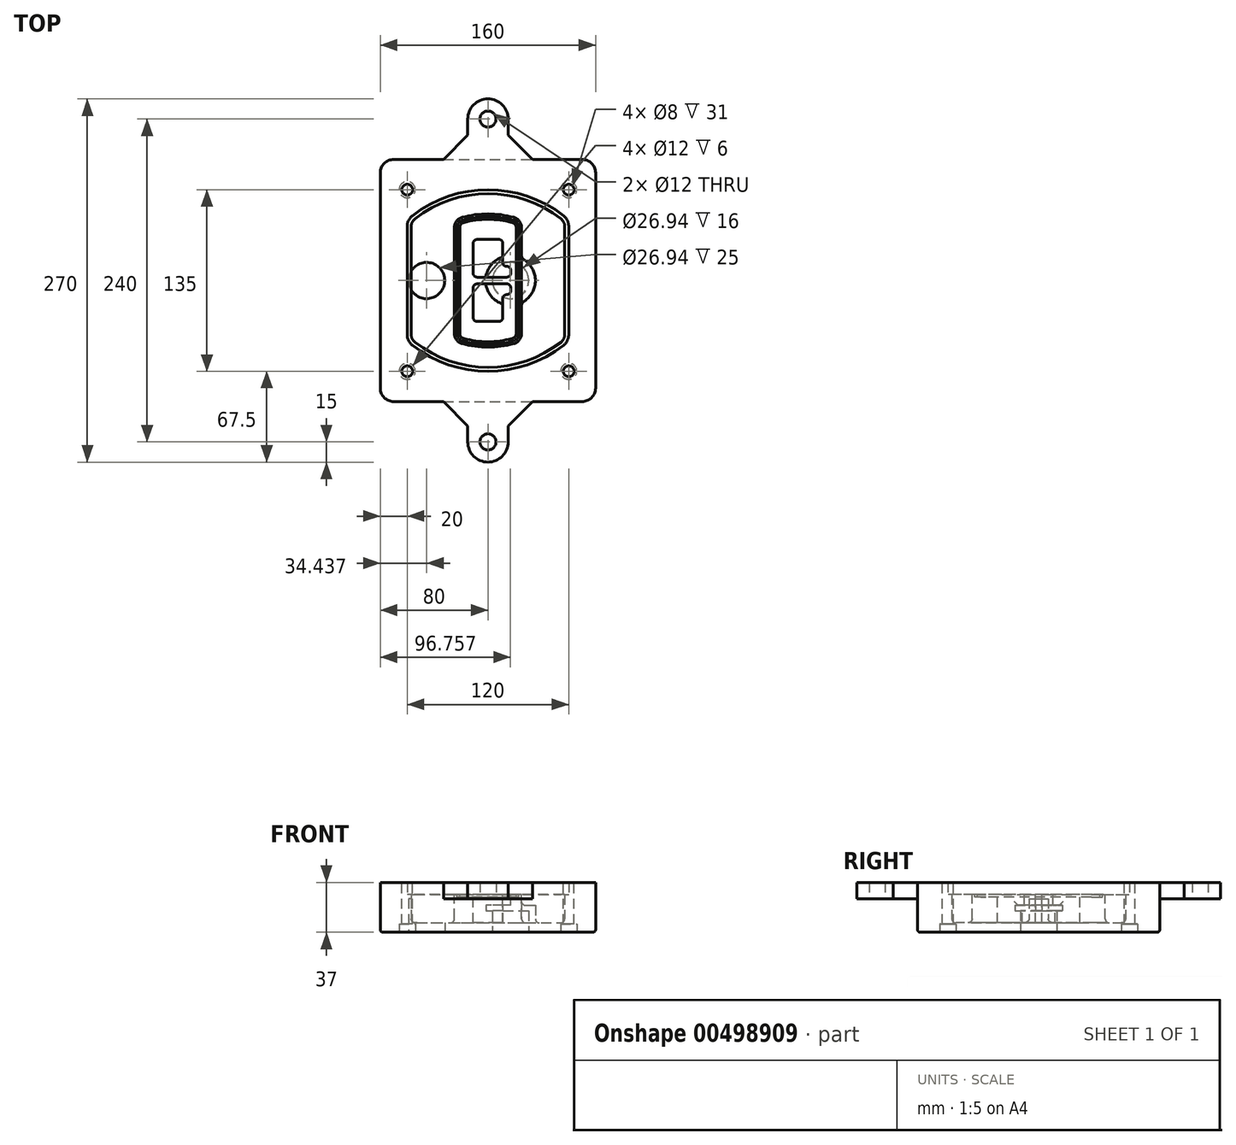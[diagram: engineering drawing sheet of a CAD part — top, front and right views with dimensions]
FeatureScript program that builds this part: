
annotation { "Feature Type Name" : "Feature", "Feature Type Description" : "" }
export const myFeature = defineFeature(function(context is Context, id is Id, definition is map)
    precondition{}
    {
        {
            var Q0;
            Q0=qCreatedBy(makeId("Top.planeOp"),FACE);
            var sketch = newSketch(context, id + "F0", { "sketchPlane" : qUnion([Q0])});
            skPoint(sketch, "E0.rect.middle", {"position": v(0, 0) * mm});
            skLineSegment(sketch, "E1.bottom", {"start": v(-70, -90) * mm, "end": v(70, -90) * mm});
            skLineSegment(sketch, "E1.top", {"start": v(-70, 90) * mm, "end": v(70, 90) * mm});
            skLineSegment(sketch, "E1.left", {"start": v(-80, -80) * mm, "end": v(-80, 80) * mm});
            skLineSegment(sketch, "E1.right", {"start": v(80, -80) * mm, "end": v(80, 80) * mm});
            skLineSegment(sketch, "E2", {"start": v(-80, 90) * mm, "end": v(80, -90) * mm, "construction": true});
            skLineSegment(sketch, "E3", {"start": v(80, 90) * mm, "end": v(-80, -90) * mm, "construction": true});
            skCircle(sketch, "E4", {"center": v(-60, 67.5) * mm, "radius": 4 * mm});
            skCircle(sketch, "E5", {"center": v(60, 67.5) * mm, "radius": 4 * mm});
            skCircle(sketch, "E6", {"center": v(60, -67.5) * mm, "radius": 4 * mm});
            skCircle(sketch, "E7", {"center": v(-60, -67.5) * mm, "radius": 4 * mm});
            skLineSegment(sketch, "E8", {"start": v(-60, 67.5) * mm, "end": v(60, 67.5) * mm, "construction": true});
            skLineSegment(sketch, "E9", {"start": v(60, 67.5) * mm, "end": v(60, -67.5) * mm, "construction": true});
            skLineSegment(sketch, "E10", {"start": v(60, -67.5) * mm, "end": v(-60, -67.5) * mm, "construction": true});
            skLineSegment(sketch, "E11", {"start": v(-60, -67.5) * mm, "end": v(-60, 67.5) * mm, "construction": true});
            skLineSegment(sketch, "E12", {"start": v(-60, 40.3) * mm, "end": v(-60, -40.3) * mm});
            skLineSegment(sketch, "E13", {"start": v(60, 40.3) * mm, "end": v(60, -40.3) * mm});
            skArc(sketch, "E14", {"start": v(56.15, 48.18) * mm, "mid": v(0, 67.5) * mm, "end": v(-56.15, 48.18) * mm});
            skArc(sketch, "E15", {"start": v(-56.15, -48.18) * mm, "mid": v(0, -67.5) * mm, "end": v(56.15, -48.18) * mm});
            skLineSegment(sketch, "E16", {"start": v(-60, 0) * mm, "end": v(60, 0) * mm, "construction": true});
            skPoint(sketch, "E17.visualSharp", {"position": v(-60, -45) * mm});
            skArc(sketch, "E17.filletArc", {"start": v(-60, -40.3) * mm, "mid": v(-58.99, -44.68) * mm, "end": v(-56.15, -48.18) * mm});
            skPoint(sketch, "E18.visualSharp", {"position": v(-60, 45) * mm});
            skArc(sketch, "E18.filletArc", {"start": v(-56.15, 48.18) * mm, "mid": v(-58.99, 44.68) * mm, "end": v(-60, 40.3) * mm});
            skPoint(sketch, "E19.visualSharp", {"position": v(60, 45) * mm});
            skArc(sketch, "E19.filletArc", {"start": v(60, 40.3) * mm, "mid": v(58.99, 44.68) * mm, "end": v(56.15, 48.18) * mm});
            skPoint(sketch, "E20.visualSharp", {"position": v(60, -45) * mm});
            skArc(sketch, "E20.filletArc", {"start": v(56.15, -48.18) * mm, "mid": v(58.99, -44.68) * mm, "end": v(60, -40.3) * mm});
            skPoint(sketch, "E21.visualSharp", {"position": v(-80, 90) * mm});
            skArc(sketch, "E21.filletArc", {"start": v(-70, 90) * mm, "mid": v(-77.07, 87.07) * mm, "end": v(-80, 80) * mm});
            skPoint(sketch, "E22.visualSharp", {"position": v(80, 90) * mm});
            skArc(sketch, "E22.filletArc", {"start": v(80, 80) * mm, "mid": v(77.07, 87.07) * mm, "end": v(70, 90) * mm});
            skPoint(sketch, "E23.visualSharp", {"position": v(80, -90) * mm});
            skArc(sketch, "E23.filletArc", {"start": v(70, -90) * mm, "mid": v(77.07, -87.07) * mm, "end": v(80, -80) * mm});
            skPoint(sketch, "E24.visualSharp", {"position": v(-80, -90) * mm});
            skArc(sketch, "E24.filletArc", {"start": v(-80, -80) * mm, "mid": v(-77.07, -87.07) * mm, "end": v(-70, -90) * mm});
            skArc(sketch, "E25.0", {"start": v(57, 40.3) * mm, "mid": v(56.3, 43.36) * mm, "end": v(54.3, 45.81) * mm});
            skLineSegment(sketch, "E25.1", {"start": v(57, 40.3) * mm, "end": v(57, -40.3) * mm});
            skArc(sketch, "E25.2", {"start": v(54.3, -45.81) * mm, "mid": v(56.3, -43.36) * mm, "end": v(57, -40.3) * mm});
            skArc(sketch, "E25.3", {"start": v(-54.3, -45.81) * mm, "mid": v(0, -64.5) * mm, "end": v(54.3, -45.81) * mm});
            skArc(sketch, "E25.4", {"start": v(-57, -40.3) * mm, "mid": v(-56.3, -43.36) * mm, "end": v(-54.3, -45.81) * mm});
            skArc(sketch, "E25.5", {"start": v(54.3, 45.81) * mm, "mid": v(0, 64.5) * mm, "end": v(-54.3, 45.81) * mm});
            skLineSegment(sketch, "E25.6", {"start": v(-57, 40.3) * mm, "end": v(-57, -40.3) * mm});
            skArc(sketch, "E25.7", {"start": v(-54.3, 45.81) * mm, "mid": v(-56.3, 43.36) * mm, "end": v(-57, 40.3) * mm});
            skArc(sketch, "E26.0", {"start": v(-58.62, 51.33) * mm, "mid": v(-62.58, 46.43) * mm, "end": v(-64, 40.3) * mm});
            skArc(sketch, "E26.1", {"start": v(58.62, 51.33) * mm, "mid": v(0, 71.5) * mm, "end": v(-58.62, 51.33) * mm});
            skArc(sketch, "E26.2", {"start": v(64, 40.3) * mm, "mid": v(62.58, 46.43) * mm, "end": v(58.62, 51.33) * mm});
            skLineSegment(sketch, "E26.3", {"start": v(64, 40.3) * mm, "end": v(64, -40.3) * mm});
            skArc(sketch, "E26.4", {"start": v(58.62, -51.33) * mm, "mid": v(62.58, -46.43) * mm, "end": v(64, -40.3) * mm});
            skLineSegment(sketch, "E26.5", {"start": v(-64, 40.3) * mm, "end": v(-64, -40.3) * mm});
            skArc(sketch, "E26.6", {"start": v(-58.62, -51.33) * mm, "mid": v(0, -71.5) * mm, "end": v(58.62, -51.33) * mm});
            skArc(sketch, "E26.7", {"start": v(-64, -40.3) * mm, "mid": v(-62.58, -46.43) * mm, "end": v(-58.62, -51.33) * mm});
            skSolve(sketch);
        }
        {
            var Q0;
            Q0=makeQuery(id+"F0.imprint","IMPRINT",FACE,{"disambiguationData":[TD([[makeQuery(id+"F0.imprint","IMPRINT",EDGE,{"derivedFrom":sQuery(id+"F0.wireOp",EDGE,"E1.bottom")}),1.0]])]});
            var Q1;
            Q1=makeQuery(id+"F0.imprint","IMPRINT",FACE,{"disambiguationData":[TD([[makeQuery(id+"F0.imprint","IMPRINT",EDGE,{"derivedFrom":sQuery(id+"F0.wireOp",EDGE,"E12")}),1.0]])]});
            var Q2;
            Q2=makeQuery(id+"F0.imprint","IMPRINT",FACE,{"disambiguationData":[TD([[makeQuery(id+"F0.imprint","IMPRINT",EDGE,{"derivedFrom":sQuery(id+"F0.wireOp",EDGE,"E25.0")}),1.0]])]});
            var Q3;
            Q3=makeQuery(id+"F0.imprint","IMPRINT",FACE,{"disambiguationData":[TD([[makeQuery(id+"F0.imprint","IMPRINT",EDGE,{"derivedFrom":sQuery(id+"F0.wireOp",EDGE,"E12")}),-1.0]])]});
            extrude(context, id + "F1", {"entities" : qUnion([Q0, Q1, Q2, Q3]), "oppositeDirection" : true, "depth" : 25 * mm});
        }
        {
            var Q0;
            Q0=makeQuery(id+"F0.imprint","IMPRINT",FACE,{"disambiguationData":[TD([[makeQuery(id+"F0.imprint","IMPRINT",EDGE,{"derivedFrom":sQuery(id+"F0.wireOp",EDGE,"E12")}),1.0]])]});
            extrude(context, id + "F2", {"entities" : qUnion([Q0]), "operationType" : NewBodyOperationType.ADD, "depth" : 3 * mm});
        }
        {
            var Q0;
            Q0=makeQuery(id+"F0.imprint","IMPRINT",FACE,{"disambiguationData":[TD([[makeQuery(id+"F0.imprint","IMPRINT",EDGE,{"derivedFrom":sQuery(id+"F0.wireOp",EDGE,"E25.0")}),1.0]])]});
            extrude(context, id + "F3", {"entities" : qUnion([Q0]), "operationType" : NewBodyOperationType.REMOVE, "oppositeDirection" : true, "depth" : 18 * mm});
        }
        {
            var Q0;
            Q0=makeQuery(id+"F2.opExtrude","CAP_FACE",FACE,{"disambiguationData":[OSD([sQuery(id+"F0.wireOp",EDGE,"E12"),sQuery(id+"F0.wireOp",EDGE,"E13"),sQuery(id+"F0.wireOp",EDGE,"E14"),sQuery(id+"F0.wireOp",EDGE,"E15"),sQuery(id+"F0.wireOp",EDGE,"E17.filletArc"),sQuery(id+"F0.wireOp",EDGE,"E18.filletArc"),sQuery(id+"F0.wireOp",EDGE,"E19.filletArc"),sQuery(id+"F0.wireOp",EDGE,"E20.filletArc"),sQuery(id+"F0.wireOp",EDGE,"E25.0"),sQuery(id+"F0.wireOp",EDGE,"E25.1"),sQuery(id+"F0.wireOp",EDGE,"E25.2"),sQuery(id+"F0.wireOp",EDGE,"E25.3"),sQuery(id+"F0.wireOp",EDGE,"E25.4"),sQuery(id+"F0.wireOp",EDGE,"E25.5"),sQuery(id+"F0.wireOp",EDGE,"E25.6"),sQuery(id+"F0.wireOp",EDGE,"E25.7")])],"isStart":false});
            var sketch = newSketch(context, id + "F4", { "sketchPlane" : qUnion([Q0])});
            skArc(sketch, "E27.0", {"start": v(-19.08, -46.97) * mm, "mid": v(0, -49.5) * mm, "end": v(19.08, -46.97) * mm});
            skArc(sketch, "E28.0", {"start": v(19.08, 46.97) * mm, "mid": v(0, 49.5) * mm, "end": v(-19.08, 46.97) * mm});
            skLineSegment(sketch, "E29", {"start": v(-25, 39.25) * mm, "end": v(-25, -39.25) * mm});
            skLineSegment(sketch, "E30", {"start": v(25, 39.25) * mm, "end": v(25, -39.25) * mm});
            skLineSegment(sketch, "E31", {"start": v(-25, 45.1) * mm, "end": v(25, 45.1) * mm, "construction": true});
            skLineSegment(sketch, "E32", {"start": v(-25, -45.1) * mm, "end": v(25, -45.1) * mm, "construction": true});
            skPoint(sketch, "E33.visualSharp", {"position": v(-25, 45.1) * mm});
            skArc(sketch, "E33.filletArc", {"start": v(-19.08, 46.97) * mm, "mid": v(-23.35, 44.11) * mm, "end": v(-25, 39.25) * mm});
            skPoint(sketch, "E34.visualSharp", {"position": v(25, 45.1) * mm});
            skArc(sketch, "E34.filletArc", {"start": v(25, 39.25) * mm, "mid": v(23.35, 44.11) * mm, "end": v(19.08, 46.97) * mm});
            skPoint(sketch, "E35.visualSharp", {"position": v(25, -45.1) * mm});
            skArc(sketch, "E35.filletArc", {"start": v(19.08, -46.97) * mm, "mid": v(23.35, -44.11) * mm, "end": v(25, -39.25) * mm});
            skPoint(sketch, "E36.visualSharp", {"position": v(-25, -45.1) * mm});
            skArc(sketch, "E36.filletArc", {"start": v(-25, -39.25) * mm, "mid": v(-23.35, -44.11) * mm, "end": v(-19.08, -46.97) * mm});
            skArc(sketch, "E37.0", {"start": v(54.3, 45.81) * mm, "mid": v(0, 64.5) * mm, "end": v(-54.3, 45.81) * mm});
            skArc(sketch, "E37.1", {"start": v(-54.3, 45.81) * mm, "mid": v(-56.3, 43.36) * mm, "end": v(-57, 40.3) * mm});
            skLineSegment(sketch, "E37.2", {"start": v(-57, 40.3) * mm, "end": v(-57, -40.3) * mm});
            skArc(sketch, "E37.3", {"start": v(-57, -40.3) * mm, "mid": v(-56.3, -43.36) * mm, "end": v(-54.3, -45.81) * mm});
            skArc(sketch, "E37.4", {"start": v(-54.3, -45.81) * mm, "mid": v(0, -64.5) * mm, "end": v(54.3, -45.81) * mm});
            skArc(sketch, "E37.5", {"start": v(54.3, -45.81) * mm, "mid": v(56.3, -43.36) * mm, "end": v(57, -40.3) * mm});
            skLineSegment(sketch, "E37.6", {"start": v(57, 40.3) * mm, "end": v(57, -40.3) * mm});
            skArc(sketch, "E37.7", {"start": v(57, 40.3) * mm, "mid": v(56.3, 43.36) * mm, "end": v(54.3, 45.81) * mm});
            skLineSegment(sketch, "E38.0", {"start": v(23, 39.25) * mm, "end": v(23, -39.25) * mm});
            skArc(sketch, "E38.1", {"start": v(18.56, -45.04) * mm, "mid": v(21.76, -42.9) * mm, "end": v(23, -39.25) * mm});
            skArc(sketch, "E38.2", {"start": v(-18.56, -45.04) * mm, "mid": v(0, -47.5) * mm, "end": v(18.56, -45.04) * mm});
            skArc(sketch, "E38.3", {"start": v(-23, -39.25) * mm, "mid": v(-21.76, -42.9) * mm, "end": v(-18.56, -45.04) * mm});
            skLineSegment(sketch, "E38.4", {"start": v(-23, 39.25) * mm, "end": v(-23, -39.25) * mm});
            skArc(sketch, "E38.5", {"start": v(23, 39.25) * mm, "mid": v(21.76, 42.9) * mm, "end": v(18.56, 45.04) * mm});
            skArc(sketch, "E38.6", {"start": v(-18.56, 45.04) * mm, "mid": v(-21.76, 42.9) * mm, "end": v(-23, 39.25) * mm});
            skArc(sketch, "E38.7", {"start": v(18.56, 45.04) * mm, "mid": v(0, 47.5) * mm, "end": v(-18.56, 45.04) * mm});
            skArc(sketch, "E39.0", {"start": v(21, 39.25) * mm, "mid": v(20.18, 41.68) * mm, "end": v(18.04, 43.1) * mm});
            skLineSegment(sketch, "E39.1", {"start": v(21, 39.25) * mm, "end": v(21, -39.25) * mm});
            skArc(sketch, "E39.2", {"start": v(18.04, -43.1) * mm, "mid": v(20.18, -41.68) * mm, "end": v(21, -39.25) * mm});
            skArc(sketch, "E39.3", {"start": v(-18.04, -43.1) * mm, "mid": v(0, -45.5) * mm, "end": v(18.04, -43.1) * mm});
            skArc(sketch, "E39.4", {"start": v(-21, -39.25) * mm, "mid": v(-20.18, -41.68) * mm, "end": v(-18.04, -43.1) * mm});
            skArc(sketch, "E39.5", {"start": v(18.04, 43.1) * mm, "mid": v(0, 45.5) * mm, "end": v(-18.04, 43.1) * mm});
            skLineSegment(sketch, "E39.6", {"start": v(-21, 39.25) * mm, "end": v(-21, -39.25) * mm});
            skArc(sketch, "E39.7", {"start": v(-18.04, 43.1) * mm, "mid": v(-20.18, 41.68) * mm, "end": v(-21, 39.25) * mm});
            skLineSegment(sketch, "E40", {"start": v(-25, 0) * mm, "end": v(25, 0) * mm, "construction": true});
            skLineSegment(sketch, "E41", {"start": v(-11, 5.5) * mm, "end": v(-11, 27.5) * mm});
            skLineSegment(sketch, "E42", {"start": v(-8, 30.5) * mm, "end": v(8, 30.5) * mm});
            skLineSegment(sketch, "E43", {"start": v(11, 27.5) * mm, "end": v(11, 13.5) * mm});
            skLineSegment(sketch, "E44", {"start": v(14, 10.5) * mm, "end": v(14, 10.5) * mm});
            skLineSegment(sketch, "E45", {"start": v(17, 7.5) * mm, "end": v(17, 5.5) * mm});
            skLineSegment(sketch, "E46", {"start": v(14, 2.5) * mm, "end": v(-8, 2.5) * mm});
            skPoint(sketch, "E47.visualSharp", {"position": v(-11, 30.5) * mm});
            skArc(sketch, "E47.filletArc", {"start": v(-8, 30.5) * mm, "mid": v(-10.12, 29.62) * mm, "end": v(-11, 27.5) * mm});
            skPoint(sketch, "E48.visualSharp", {"position": v(11, 30.5) * mm});
            skArc(sketch, "E48.filletArc", {"start": v(11, 27.5) * mm, "mid": v(10.12, 29.62) * mm, "end": v(8, 30.5) * mm});
            skPoint(sketch, "E49.visualSharp", {"position": v(11, 10.5) * mm});
            skArc(sketch, "E49.filletArc", {"start": v(11, 13.5) * mm, "mid": v(11.88, 11.38) * mm, "end": v(14, 10.5) * mm});
            skPoint(sketch, "E50.visualSharp", {"position": v(17, 10.5) * mm});
            skArc(sketch, "E50.filletArc", {"start": v(17, 7.5) * mm, "mid": v(16.12, 9.62) * mm, "end": v(14, 10.5) * mm});
            skPoint(sketch, "E51.visualSharp", {"position": v(17, 2.5) * mm});
            skArc(sketch, "E51.filletArc", {"start": v(14, 2.5) * mm, "mid": v(16.12, 3.38) * mm, "end": v(17, 5.5) * mm});
            skPoint(sketch, "E52.visualSharp", {"position": v(-11, 2.5) * mm});
            skArc(sketch, "E52.filletArc", {"start": v(-11, 5.5) * mm, "mid": v(-10.12, 3.38) * mm, "end": v(-8, 2.5) * mm});
            skLineSegment(sketch, "E53.0.MirrorCS", {"start": v(14, -2.5) * mm, "end": v(-8, -2.5) * mm});
            skArc(sketch, "E54.0.MirrorCS", {"start": v(-11, -5.5) * mm, "mid": v(-10.12, -3.38) * mm, "end": v(-8, -2.5) * mm});
            skLineSegment(sketch, "E55.0.MirrorCS", {"start": v(-11, -5.5) * mm, "end": v(-11, -27.5) * mm});
            skArc(sketch, "E56.0.MirrorCS", {"start": v(-8, -30.5) * mm, "mid": v(-10.12, -29.62) * mm, "end": v(-11, -27.5) * mm});
            skLineSegment(sketch, "E57.0.MirrorCS", {"start": v(-8, -30.5) * mm, "end": v(8, -30.5) * mm});
            skArc(sketch, "E58.0.MirrorCS", {"start": v(11, -27.5) * mm, "mid": v(10.12, -29.62) * mm, "end": v(8, -30.5) * mm});
            skLineSegment(sketch, "E59.0.MirrorCS", {"start": v(11, -27.5) * mm, "end": v(11, -13.5) * mm});
            skArc(sketch, "E60.0.MirrorCS", {"start": v(11, -13.5) * mm, "mid": v(11.88, -11.38) * mm, "end": v(14, -10.5) * mm});
            skArc(sketch, "E61.0.MirrorCS", {"start": v(17, -7.5) * mm, "mid": v(16.12, -9.62) * mm, "end": v(14, -10.5) * mm});
            skLineSegment(sketch, "E62.0.MirrorCS", {"start": v(17, -7.5) * mm, "end": v(17, -5.5) * mm});
            skArc(sketch, "E63.0.MirrorCS", {"start": v(14, -2.5) * mm, "mid": v(16.12, -3.38) * mm, "end": v(17, -5.5) * mm});
            skSolve(sketch);
        }
        {
            var Q0;
            Q0=makeQuery(id+"F4.imprint","IMPRINT",FACE,{"disambiguationData":[TD([[makeQuery(id+"F4.imprint","IMPRINT",EDGE,{"derivedFrom":sQuery(id+"F4.wireOp",EDGE,"E27.0")}),1.0]])]});
            var Q1;
            Q1=makeQuery(id+"F4.imprint","IMPRINT",FACE,{"disambiguationData":[TD([[makeQuery(id+"F4.imprint","IMPRINT",EDGE,{"derivedFrom":sQuery(id+"F4.wireOp",EDGE,"E38.0")}),-1.0]])]});
            var Q2;
            Q2=makeQuery(id+"F4.imprint","IMPRINT",FACE,{"disambiguationData":[TD([[makeQuery(id+"F4.imprint","IMPRINT",EDGE,{"derivedFrom":sQuery(id+"F4.wireOp",EDGE,"E39.0")}),1.0]])]});
            extrude(context, id + "F5", {"entities" : qUnion([Q0, Q1, Q2]), "operationType" : NewBodyOperationType.ADD, "endBound" : BoundingType.UP_TO_NEXT, "oppositeDirection" : true, "depth" : 25 * mm});
        }
        {
            var Q0;
            Q0=makeQuery(id+"F4.imprint","IMPRINT",FACE,{"disambiguationData":[TD([[makeQuery(id+"F4.imprint","IMPRINT",EDGE,{"derivedFrom":sQuery(id+"F4.wireOp",EDGE,"E38.0")}),-1.0]])]});
            extrude(context, id + "F6", {"entities" : qUnion([Q0]), "operationType" : NewBodyOperationType.REMOVE, "oppositeDirection" : true, "depth" : 2 * mm});
        }
        {
            var Q0;
            Q0=makeQuery(id+"F1.opExtrude","CAP_FACE",FACE,{"disambiguationData":[OSD([sQuery(id+"F0.wireOp",EDGE,"E1.bottom"),sQuery(id+"F0.wireOp",EDGE,"E1.top"),sQuery(id+"F0.wireOp",EDGE,"E1.left"),sQuery(id+"F0.wireOp",EDGE,"E1.right"),sQuery(id+"F0.wireOp",EDGE,"E4"),sQuery(id+"F0.wireOp",EDGE,"E5"),sQuery(id+"F0.wireOp",EDGE,"E6"),sQuery(id+"F0.wireOp",EDGE,"E7"),sQuery(id+"F0.wireOp",EDGE,"E21.filletArc"),sQuery(id+"F0.wireOp",EDGE,"E22.filletArc"),sQuery(id+"F0.wireOp",EDGE,"E23.filletArc"),sQuery(id+"F0.wireOp",EDGE,"E24.filletArc")])],"isStart":false});
            var sketch = newSketch(context, id + "F7", { "sketchPlane" : qUnion([Q0])});
            skCircle(sketch, "E64", {"center": v(16.76, 0) * mm, "radius": 13.47 * mm});
            skCircle(sketch, "E65", {"center": v(-45.56, 0) * mm, "radius": 13.47 * mm});
            skLineSegment(sketch, "E66", {"start": v(80, 0) * mm, "end": v(-80, 0) * mm});
            skCircle(sketch, "E67", {"center": v(16.76, 0) * mm, "radius": 18.47 * mm});
            skCircle(sketch, "E68", {"center": v(60, -67.5) * mm, "radius": 6 * mm});
            skCircle(sketch, "E69", {"center": v(-60, -67.5) * mm, "radius": 6 * mm});
            skCircle(sketch, "E70", {"center": v(-60, 67.5) * mm, "radius": 6 * mm});
            skCircle(sketch, "E71", {"center": v(60, 67.5) * mm, "radius": 6 * mm});
            skSolve(sketch);
        }
        {
            var Q0;
            {var subQ1=sQuery(id+"F7.wireOp",EDGE,"E66");var subQ4=sQuery(id+"F7.wireOp",EDGE,"E64");var subQ6=makeQuery(id+"F7.imprint","INTERSECT",VERTEX,{"disambiguationData":[OD(0.0)],"derivedFrom":[subQ4,subQ1]});Q0=makeQuery(id+"F7.imprint","IMPRINT",FACE,{"disambiguationData":[TD([[makeQuery(id+"F7.imprint","IMPRINT",EDGE,{"disambiguationData":[TD([[subQ6,-1.0]])],"derivedFrom":subQ4}),-1.0]])]});}
            var Q1;
            {var subQ0=sQuery(id+"F7.wireOp",EDGE,"E66");var subQ1=sQuery(id+"F7.wireOp",EDGE,"E64");var subQ3=makeQuery(id+"F7.imprint","INTERSECT",VERTEX,{"disambiguationData":[OD(0.0)],"derivedFrom":[subQ1,subQ0]});Q1=makeQuery(id+"F7.imprint","IMPRINT",FACE,{"disambiguationData":[TD([[makeQuery(id+"F7.imprint","IMPRINT",EDGE,{"disambiguationData":[TD([[subQ3,-1.0]])],"derivedFrom":subQ1}),1.0]])]});}
            var Q2;
            {var subQ0=sQuery(id+"F7.wireOp",EDGE,"E66");var subQ1=sQuery(id+"F7.wireOp",EDGE,"E64");var subQ3=makeQuery(id+"F7.imprint","INTERSECT",VERTEX,{"disambiguationData":[OD(0.0)],"derivedFrom":[subQ1,subQ0]});Q2=makeQuery(id+"F7.imprint","IMPRINT",FACE,{"disambiguationData":[TD([[makeQuery(id+"F7.imprint","IMPRINT",EDGE,{"disambiguationData":[TD([[subQ3,1.0]])],"derivedFrom":subQ1}),1.0]])]});}
            var Q3;
            {var subQ1=sQuery(id+"F7.wireOp",EDGE,"E66");var subQ4=sQuery(id+"F7.wireOp",EDGE,"E64");var subQ6=makeQuery(id+"F7.imprint","INTERSECT",VERTEX,{"disambiguationData":[OD(0.0)],"derivedFrom":[subQ4,subQ1]});Q3=makeQuery(id+"F7.imprint","IMPRINT",FACE,{"disambiguationData":[TD([[makeQuery(id+"F7.imprint","IMPRINT",EDGE,{"disambiguationData":[TD([[subQ6,1.0]])],"derivedFrom":subQ4}),-1.0]])]});}
            extrude(context, id + "F8", {"entities" : qUnion([Q0, Q1, Q2, Q3]), "operationType" : NewBodyOperationType.ADD, "oppositeDirection" : true, "depth" : 20 * mm});
        }
        {
            var Q0;
            {var subQ0=sQuery(id+"F7.wireOp",EDGE,"E66");var subQ1=sQuery(id+"F7.wireOp",EDGE,"E64");var subQ3=makeQuery(id+"F7.imprint","INTERSECT",VERTEX,{"disambiguationData":[OD(0.0)],"derivedFrom":[subQ1,subQ0]});Q0=makeQuery(id+"F7.imprint","IMPRINT",FACE,{"disambiguationData":[TD([[makeQuery(id+"F7.imprint","IMPRINT",EDGE,{"disambiguationData":[TD([[subQ3,-1.0]])],"derivedFrom":subQ1}),1.0]])]});}
            var Q1;
            {var subQ0=sQuery(id+"F7.wireOp",EDGE,"E66");var subQ1=sQuery(id+"F7.wireOp",EDGE,"E64");var subQ3=makeQuery(id+"F7.imprint","INTERSECT",VERTEX,{"disambiguationData":[OD(0.0)],"derivedFrom":[subQ1,subQ0]});Q1=makeQuery(id+"F7.imprint","IMPRINT",FACE,{"disambiguationData":[TD([[makeQuery(id+"F7.imprint","IMPRINT",EDGE,{"disambiguationData":[TD([[subQ3,1.0]])],"derivedFrom":subQ1}),1.0]])]});}
            extrude(context, id + "F9", {"entities" : qUnion([Q0, Q1]), "operationType" : NewBodyOperationType.REMOVE, "oppositeDirection" : true, "depth" : 16 * mm});
        }
        {
            var Q0;
            {var subQ0=sQuery(id+"F7.wireOp",EDGE,"E66");var subQ1=sQuery(id+"F7.wireOp",EDGE,"E65");var subQ3=makeQuery(id+"F7.imprint","INTERSECT",VERTEX,{"disambiguationData":[OD(0.0)],"derivedFrom":[subQ1,subQ0]});Q0=makeQuery(id+"F7.imprint","IMPRINT",FACE,{"disambiguationData":[TD([[makeQuery(id+"F7.imprint","IMPRINT",EDGE,{"disambiguationData":[TD([[subQ3,-1.0]])],"derivedFrom":subQ1}),1.0]])]});}
            var Q1;
            {var subQ0=sQuery(id+"F7.wireOp",EDGE,"E66");var subQ1=sQuery(id+"F7.wireOp",EDGE,"E65");var subQ3=makeQuery(id+"F7.imprint","INTERSECT",VERTEX,{"disambiguationData":[OD(0.0)],"derivedFrom":[subQ1,subQ0]});Q1=makeQuery(id+"F7.imprint","IMPRINT",FACE,{"disambiguationData":[TD([[makeQuery(id+"F7.imprint","IMPRINT",EDGE,{"disambiguationData":[TD([[subQ3,1.0]])],"derivedFrom":subQ1}),1.0]])]});}
            extrude(context, id + "F10", {"entities" : qUnion([Q0, Q1]), "operationType" : NewBodyOperationType.REMOVE, "oppositeDirection" : true, "depth" : 25 * mm});
        }
        {
            var Q0;
            Q0=makeQuery(id+"F7.imprint","IMPRINT",FACE,{"disambiguationData":[TD([[makeQuery(id+"F7.imprint","IMPRINT",EDGE,{"derivedFrom":sQuery(id+"F7.wireOp",EDGE,"E68")}),1.0]])]});
            var Q1;
            Q1=makeQuery(id+"F7.imprint","IMPRINT",FACE,{"disambiguationData":[TD([[makeQuery(id+"F7.imprint","IMPRINT",EDGE,{"derivedFrom":makeQuery(id+"F1.opExtrude","CAP_EDGE",EDGE,{"disambiguationData":[OSD([sQuery(id+"F0.wireOp",EDGE,"E5")])],"isStart":false})}),-1.0]])]});
            var Q2;
            Q2=makeQuery(id+"F7.imprint","IMPRINT",FACE,{"disambiguationData":[TD([[makeQuery(id+"F7.imprint","IMPRINT",EDGE,{"derivedFrom":sQuery(id+"F7.wireOp",EDGE,"E69")}),1.0]])]});
            var Q3;
            Q3=makeQuery(id+"F7.imprint","IMPRINT",FACE,{"disambiguationData":[TD([[makeQuery(id+"F7.imprint","IMPRINT",EDGE,{"derivedFrom":makeQuery(id+"F1.opExtrude","CAP_EDGE",EDGE,{"disambiguationData":[OSD([sQuery(id+"F0.wireOp",EDGE,"E4")])],"isStart":false})}),-1.0]])]});
            var Q4;
            Q4=makeQuery(id+"F7.imprint","IMPRINT",FACE,{"disambiguationData":[TD([[makeQuery(id+"F7.imprint","IMPRINT",EDGE,{"derivedFrom":sQuery(id+"F7.wireOp",EDGE,"E70")}),1.0]])]});
            var Q5;
            Q5=makeQuery(id+"F7.imprint","IMPRINT",FACE,{"disambiguationData":[TD([[makeQuery(id+"F7.imprint","IMPRINT",EDGE,{"derivedFrom":makeQuery(id+"F1.opExtrude","CAP_EDGE",EDGE,{"disambiguationData":[OSD([sQuery(id+"F0.wireOp",EDGE,"E7")])],"isStart":false})}),-1.0]])]});
            var Q6;
            Q6=makeQuery(id+"F7.imprint","IMPRINT",FACE,{"disambiguationData":[TD([[makeQuery(id+"F7.imprint","IMPRINT",EDGE,{"derivedFrom":sQuery(id+"F7.wireOp",EDGE,"E71")}),1.0]])]});
            var Q7;
            Q7=makeQuery(id+"F7.imprint","IMPRINT",FACE,{"disambiguationData":[TD([[makeQuery(id+"F7.imprint","IMPRINT",EDGE,{"derivedFrom":makeQuery(id+"F1.opExtrude","CAP_EDGE",EDGE,{"disambiguationData":[OSD([sQuery(id+"F0.wireOp",EDGE,"E6")])],"isStart":false})}),-1.0]])]});
            extrude(context, id + "F11", {"entities" : qUnion([Q0, Q1, Q2, Q3, Q4, Q5, Q6, Q7]), "operationType" : NewBodyOperationType.REMOVE, "oppositeDirection" : true, "depth" : 6 * mm});
        }
        {
            var Q0;
            Q0=makeQuery(id+"F9.boolean.opBoolean","COPY",FACE,{"derivedFrom":makeQuery(id+"F9.opExtrude","CAP_FACE",FACE,{"disambiguationData":[OSD([sQuery(id+"F7.wireOp",EDGE,"E64")])],"isStart":false})});
            var sketch = newSketch(context, id + "F12", { "sketchPlane" : qUnion([Q0])});
            skArc(sketch, "E72.0", {"start": v(11, 17.55) * mm, "mid": v(2.57, 11.82) * mm, "end": v(-1.54, 2.5) * mm});
            skArc(sketch, "E72.1", {"start": v(-1.54, -2.5) * mm, "mid": v(2.57, -11.82) * mm, "end": v(11, -17.55) * mm});
            skLineSegment(sketch, "E73", {"start": v(-1.54, -2.5) * mm, "end": v(14, -2.5) * mm});
            skLineSegment(sketch, "E74.0", {"start": v(14, 2.5) * mm, "end": v(-1.54, 2.5) * mm});
            skArc(sketch, "E74.1", {"start": v(14, 2.5) * mm, "mid": v(16.12, 3.38) * mm, "end": v(17, 5.5) * mm});
            skLineSegment(sketch, "E74.2", {"start": v(17, 7.5) * mm, "end": v(17, 5.5) * mm});
            skArc(sketch, "E74.3", {"start": v(17, 7.5) * mm, "mid": v(16.12, 9.62) * mm, "end": v(14, 10.5) * mm});
            skArc(sketch, "E74.4", {"start": v(11, 13.5) * mm, "mid": v(11.88, 11.38) * mm, "end": v(14, 10.5) * mm});
            skLineSegment(sketch, "E74.5", {"start": v(11, 17.55) * mm, "end": v(11, 13.5) * mm});
            skLineSegment(sketch, "E74.7", {"start": v(14, -2.5) * mm, "end": v(-1.54, -2.5) * mm});
            skArc(sketch, "E74.8", {"start": v(14, -2.5) * mm, "mid": v(16.12, -3.38) * mm, "end": v(17, -5.5) * mm});
            skLineSegment(sketch, "E74.9", {"start": v(17, -7.5) * mm, "end": v(17, -5.5) * mm});
            skArc(sketch, "E74.10", {"start": v(17, -7.5) * mm, "mid": v(16.12, -9.62) * mm, "end": v(14, -10.5) * mm});
            skArc(sketch, "E74.11", {"start": v(11, -13.5) * mm, "mid": v(11.88, -11.38) * mm, "end": v(14, -10.5) * mm});
            skLineSegment(sketch, "E74.12", {"start": v(11, -17.55) * mm, "end": v(11, -13.5) * mm});
            skPoint(sketch, "E75.orphan", {"position": v(11, -27.5) * mm});
            skPoint(sketch, "E76.orphan", {"position": v(-8, -2.5) * mm});
            skPoint(sketch, "E77.orphan", {"position": v(-8, 2.5) * mm});
            skPoint(sketch, "E78.orphan", {"position": v(11, 27.5) * mm});
            skSolve(sketch);
        }
        {
            var Q0;
            {var subQ7=sQuery(id+"F12.wireOp",EDGE,"E72.0");var subQ14=sQuery(id+"F12.wireOp",EDGE,"E72.1");var subQ16=sQuery(id+"F12.wireOp",EDGE,"E74.1");var subQ18=sQuery(id+"F12.wireOp",EDGE,"E74.8");Q0=qUnion([makeQuery(id+"F12.imprint","IMPRINT",FACE,{"disambiguationData":[TD([[makeQuery(id+"F12.imprint","IMPRINT",EDGE,{"derivedFrom":subQ7}),1.0]])]}),makeQuery(id+"F12.imprint","IMPRINT",FACE,{"disambiguationData":[TD([[makeQuery(id+"F12.imprint","IMPRINT",EDGE,{"derivedFrom":subQ14}),1.0]])]}),makeQuery(id+"F12.imprint","IMPRINT",FACE,{"disambiguationData":[TD([[makeQuery(id+"F12.imprint","IMPRINT",EDGE,{"derivedFrom":subQ16}),1.0]])]}),makeQuery(id+"F12.imprint","IMPRINT",FACE,{"disambiguationData":[TD([[makeQuery(id+"F12.imprint","IMPRINT",EDGE,{"derivedFrom":subQ18}),-1.0]])]})]);}
            var Q1;
            Q1=makeQuery(id+"F5.boolean.opBoolean","SPLIT",FACE,{"disambiguationData":[TD([makeQuery(id+"F5.opExtrude","SWEPT_FACE",FACE,{"disambiguationData":[OSD([sQuery(id+"F4.wireOp",EDGE,"E41")])]})])],"derivedFrom":makeQuery(id+"F3.boolean.opBoolean","COPY",FACE,{"derivedFrom":makeQuery(id+"F3.opExtrude","CAP_FACE",FACE,{"disambiguationData":[OSD([sQuery(id+"F0.wireOp",EDGE,"E25.0"),sQuery(id+"F0.wireOp",EDGE,"E25.1"),sQuery(id+"F0.wireOp",EDGE,"E25.2"),sQuery(id+"F0.wireOp",EDGE,"E25.3"),sQuery(id+"F0.wireOp",EDGE,"E25.4"),sQuery(id+"F0.wireOp",EDGE,"E25.5"),sQuery(id+"F0.wireOp",EDGE,"E25.6"),sQuery(id+"F0.wireOp",EDGE,"E25.7")])],"isStart":false})})});
            extrude(context, id + "F13", {"entities" : qUnion([Q0]), "operationType" : NewBodyOperationType.REMOVE, "endBound" : BoundingType.UP_TO_SURFACE, "endBoundEntityFace" : qUnion([Q1]), "depth" : 25 * mm});
        }
        {
            var Q0;
            Q0=makeQuery(id+"F3.boolean.opBoolean","COPY",EDGE,{"derivedFrom":makeQuery(id+"F3.opExtrude","CAP_EDGE",EDGE,{"disambiguationData":[OSD([sQuery(id+"F0.wireOp",EDGE,"E25.6")])],"isStart":false})});
            var Q1;
            Q1=makeQuery(id+"F8.boolean.opBoolean","INTERSECT",EDGE,{"derivedFrom":[makeQuery(id+"F5.opExtrude","SWEPT_FACE",FACE,{"disambiguationData":[OSD([sQuery(id+"F4.wireOp",EDGE,"E30")])]}),makeQuery(id+"F8.opExtrude","CAP_FACE",FACE,{"disambiguationData":[OSD([sQuery(id+"F7.wireOp",EDGE,"E67")])],"isStart":false})]});
            var Q2;
            Q2=makeQuery(id+"F8.boolean.opBoolean","INTERSECT",EDGE,{"disambiguationData":[OD(1.0)],"derivedFrom":[makeQuery(id+"F5.opExtrude","SWEPT_FACE",FACE,{"disambiguationData":[OSD([sQuery(id+"F4.wireOp",EDGE,"E30")])]}),makeQuery(id+"F8.opExtrude","SWEPT_FACE",FACE,{"disambiguationData":[OSD([sQuery(id+"F7.wireOp",EDGE,"E67")])]})]});
            var Q3;
            {var subQ0=sQuery(id+"F4.wireOp",EDGE,"E30");Q3=makeQuery(id+"F8.boolean.opBoolean","SPLIT",EDGE,{"disambiguationData":[TD([makeQuery(id+"F5.opExtrude","SWEPT_FACE",FACE,{"disambiguationData":[OSD([sQuery(id+"F4.wireOp",EDGE,"E35.filletArc")])]})])],"derivedFrom":makeQuery(id+"F5.opExtrude","CAP_EDGE",EDGE,{"disambiguationData":[OSD([subQ0])],"isStart":false})});}
            var Q4;
            {var subQ0=sQuery(id+"F0.wireOp",EDGE,"E25.7");var subQ1=sQuery(id+"F0.wireOp",EDGE,"E25.1");var subQ2=sQuery(id+"F0.wireOp",EDGE,"E25.6");var subQ3=sQuery(id+"F0.wireOp",EDGE,"E25.5");var subQ4=sQuery(id+"F0.wireOp",EDGE,"E25.4");var subQ5=sQuery(id+"F0.wireOp",EDGE,"E25.0");var subQ6=sQuery(id+"F0.wireOp",EDGE,"E25.2");var subQ7=sQuery(id+"F0.wireOp",EDGE,"E25.3");Q4=makeQuery(id+"F8.boolean.opBoolean","INTERSECT",EDGE,{"derivedFrom":[makeQuery(id+"F5.boolean.opBoolean","SPLIT",FACE,{"disambiguationData":[TD([makeQuery(id+"F2.opExtrude","SWEPT_FACE",FACE,{"disambiguationData":[OSD([subQ5])]})])],"derivedFrom":makeQuery(id+"F3.boolean.opBoolean","COPY",FACE,{"derivedFrom":makeQuery(id+"F3.opExtrude","CAP_FACE",FACE,{"disambiguationData":[OSD([subQ5,subQ1,subQ6,subQ7,subQ4,subQ3,subQ2,subQ0])],"isStart":false})})}),makeQuery(id+"F8.opExtrude","SWEPT_FACE",FACE,{"disambiguationData":[OSD([sQuery(id+"F7.wireOp",EDGE,"E67")])]})]});}
            var Q5;
            Q5=makeQuery(id+"F8.boolean.opBoolean","INTERSECT",EDGE,{"disambiguationData":[OD(0.0)],"derivedFrom":[makeQuery(id+"F5.opExtrude","SWEPT_FACE",FACE,{"disambiguationData":[OSD([sQuery(id+"F4.wireOp",EDGE,"E30")])]}),makeQuery(id+"F8.opExtrude","SWEPT_FACE",FACE,{"disambiguationData":[OSD([sQuery(id+"F7.wireOp",EDGE,"E67")])]})]});
            fillet(context, id + "F14", {"entities" : qUnion([Q0, Q1, Q2, Q3, Q4, Q5]), "radius" : 3 * mm, "tangentPropagation" : true, "allowEdgeOverflow" : false});
        }
        {
            var Q0;
            Q0=makeQuery(id+"F1.opExtrude","CAP_EDGE",EDGE,{"disambiguationData":[OSD([sQuery(id+"F0.wireOp",EDGE,"E1.bottom")])],"isStart":false});
            fillet(context, id + "F15", {"entities" : qUnion([Q0]), "radius" : 2 * mm, "tangentPropagation" : true, "allowEdgeOverflow" : false});
        }
        {
            var Q0;
            {var subQ0=sQuery(id+"F0.wireOp",EDGE,"E21.filletArc");var subQ1=sQuery(id+"F0.wireOp",EDGE,"E7");var subQ2=sQuery(id+"F0.wireOp",EDGE,"E6");var subQ3=sQuery(id+"F0.wireOp",EDGE,"E5");var subQ4=sQuery(id+"F0.wireOp",EDGE,"E4");var subQ5=sQuery(id+"F0.wireOp",EDGE,"E22.filletArc");var subQ6=sQuery(id+"F0.wireOp",EDGE,"E1.bottom");var subQ7=sQuery(id+"F0.wireOp",EDGE,"E1.right");var subQ8=sQuery(id+"F0.wireOp",EDGE,"E1.top");var subQ9=sQuery(id+"F0.wireOp",EDGE,"E1.left");var subQ10=sQuery(id+"F0.wireOp",EDGE,"E23.filletArc");var subQ11=sQuery(id+"F0.wireOp",EDGE,"E24.filletArc");Q0=makeQuery(id+"F2.boolean.opBoolean","SPLIT",FACE,{"disambiguationData":[TD([makeQuery(id+"F1.opExtrude","SWEPT_FACE",FACE,{"disambiguationData":[OSD([subQ6])]})])],"derivedFrom":makeQuery(id+"F1.opExtrude","CAP_FACE",FACE,{"disambiguationData":[OSD([subQ6,subQ8,subQ9,subQ7,subQ4,subQ3,subQ2,subQ1,subQ0,subQ5,subQ10,subQ11])],"isStart":true})});}
            var sketch = newSketch(context, id + "F16", { "sketchPlane" : qUnion([Q0])});
            skCircle(sketch, "E79", {"center": v(0, 120) * mm, "radius": 6 * mm});
            skLineSegment(sketch, "E80", {"start": v(0, 120) * mm, "end": v(0, 90) * mm, "construction": true});
            skArc(sketch, "E81", {"start": v(15, 120) * mm, "mid": v(0, 135) * mm, "end": v(-15, 120) * mm});
            skLineSegment(sketch, "E82", {"start": v(-15, 120) * mm, "end": v(-15, 108) * mm});
            skLineSegment(sketch, "E83", {"start": v(15, 120) * mm, "end": v(15, 108) * mm});
            skLineSegment(sketch, "E84", {"start": v(-15, 108) * mm, "end": v(-33, 90) * mm});
            skLineSegment(sketch, "E85", {"start": v(15, 108) * mm, "end": v(33, 90) * mm});
            skLineSegment(sketch, "E86", {"start": v(-80, 0) * mm, "end": v(80, 0) * mm, "construction": true});
            skLineSegment(sketch, "E87.MirrorCS", {"start": v(15, -108) * mm, "end": v(33, -90) * mm});
            skLineSegment(sketch, "E88.MirrorCS", {"start": v(-15, -108) * mm, "end": v(-33, -90) * mm});
            skLineSegment(sketch, "E89.MirrorCS", {"start": v(-15, -120) * mm, "end": v(-15, -108) * mm});
            skArc(sketch, "E90.MirrorCS", {"start": v(15, -120) * mm, "mid": v(0, -135) * mm, "end": v(-15, -120) * mm});
            skLineSegment(sketch, "E91.MirrorCS", {"start": v(15, -120) * mm, "end": v(15, -108) * mm});
            skCircle(sketch, "E92.MirrorC", {"center": v(0, -120) * mm, "radius": 6 * mm});
            skLineSegment(sketch, "E93.MirrorCS", {"start": v(0, -120) * mm, "end": v(0, -90) * mm, "construction": true});
            skSolve(sketch);
        }
        {
            var Q0;
            Q0=makeQuery(id+"F16.imprint","IMPRINT",FACE,{"disambiguationData":[TD([[makeQuery(id+"F16.imprint","IMPRINT",EDGE,{"derivedFrom":sQuery(id+"F16.wireOp",EDGE,"E79")}),-1.0]])]});
            var Q1;
            Q1=makeQuery(id+"F16.imprint","IMPRINT",FACE,{"disambiguationData":[TD([[makeQuery(id+"F16.imprint","IMPRINT",EDGE,{"derivedFrom":makeQuery(id+"F1.opExtrude","CAP_EDGE",EDGE,{"disambiguationData":[OSD([sQuery(id+"F0.wireOp",EDGE,"E1.left")])],"isStart":true})}),-1.0]])]});
            var Q2;
            {var subQ1=sQuery(id+"F16.wireOp",EDGE,"E87.MirrorCS");Q2=makeQuery(id+"F16.imprint","IMPRINT",FACE,{"disambiguationData":[TD([[makeQuery(id+"F16.imprint","IMPRINT",EDGE,{"derivedFrom":subQ1}),1.0]])]});}
            extrude(context, id + "F17", {"entities" : qUnion([Q0, Q1, Q2]), "operationType" : NewBodyOperationType.ADD, "depth" : 12 * mm, "offsetDistance" : 25 * mm});
        }
    });
